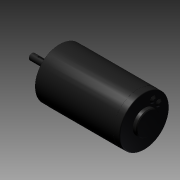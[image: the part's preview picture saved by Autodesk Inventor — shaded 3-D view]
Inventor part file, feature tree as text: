
AUTODESK INVENTOR PART (.ipt)
format: ipt  version: 2014 SP1 (Build 180222100, 222)  size: 139,264 bytes
history: native  units: in
note: dims shown in document units (in); Inventor stores cm internally (conversion verified against a paired STEP export)
features: chamfer x1, imported_body x1
ambient origin geometry x8: Origin, YZ Plane, XZ Plane, XY Plane, X Axis, Y Axis, Z Axis, Center Point
bodies: Body1 (feature_tree)
feature tree (2):
  chamfer  "Chamfer3"  [1 undecoded]
  imported_body  "Base1"
note: 1 required parameter value undecoded (feature->parameter linkage not recoverable at this tier; creation-order binding heuristic only, values carry confidence <= 0.55)
